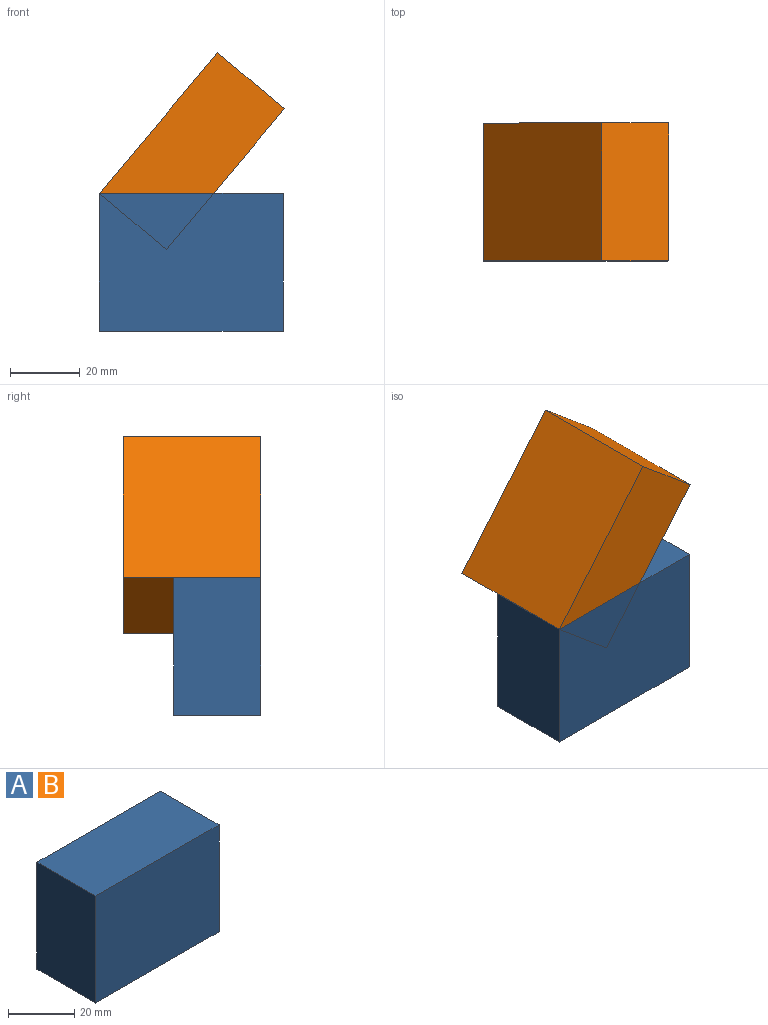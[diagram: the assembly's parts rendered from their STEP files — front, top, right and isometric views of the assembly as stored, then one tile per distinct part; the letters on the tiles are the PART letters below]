
ASSEMBLY  parts=2 mates=1
PART A: 6 faces, bbox 52.6x25x39.5 mm
  f0: plane 52.6x25mm, normal (0,0,1), area 1315.1mm2, adj f1,f3,f4,f5
  f1: plane 39.46x25mm, normal (-1,0,0), area 986.6mm2, adj f0,f2,f4,f5
  f2: plane 52.6x25mm, normal (0,0,-1), area 1315.1mm2, adj f1,f3,f4,f5
  f3: plane 39.46x25mm, normal (1,0,0), area 986.6mm2, adj f0,f2,f4,f5
  f4: plane 52.6x39.46mm, normal (0,-1,0), area 2075.9mm2, adj f0,f1,f2,f3
  f5: plane 52.6x39.46mm, normal (0,1,0), area 2075.9mm2, adj f0,f1,f2,f3
PART B: same geometry as A
PLACE A t=(29.51,33.7,-14.73)mm
PLACE B rot(axis=(0.83,-0.39,0.39),100.3deg) t=(8.16,78.39,100.74)mm
MATE revolute B.f0 <-> A.f4  axis (0,-1,0) through (-30.26,8.7,54.96)mm
